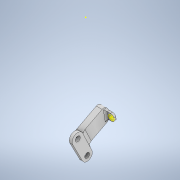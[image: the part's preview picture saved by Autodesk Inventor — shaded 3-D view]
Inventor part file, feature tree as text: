
AUTODESK INVENTOR PART (.ipt)
format: ipt  version: 2020 (Build 240168000, 168)  size: 167,936 bytes
history: native  units: in
note: dims shown in document units (in); Inventor stores cm internally (conversion verified against a paired STEP export)
features: other x3, sketch x1
ambient origin geometry x8: Origin, YZ Plane, XZ Plane, XY Plane, X Axis, Y Axis, Z Axis, Center Point
bodies: Solid1 (feature_tree)
feature tree (4):
  other  "Kauri camera mount.ipt"
  other  "Solid3::Kauri camera mount.ipt"
  other  "TaggingFeature1"
  sketch  "Sketch7"  dims[d0=0.3937in]
